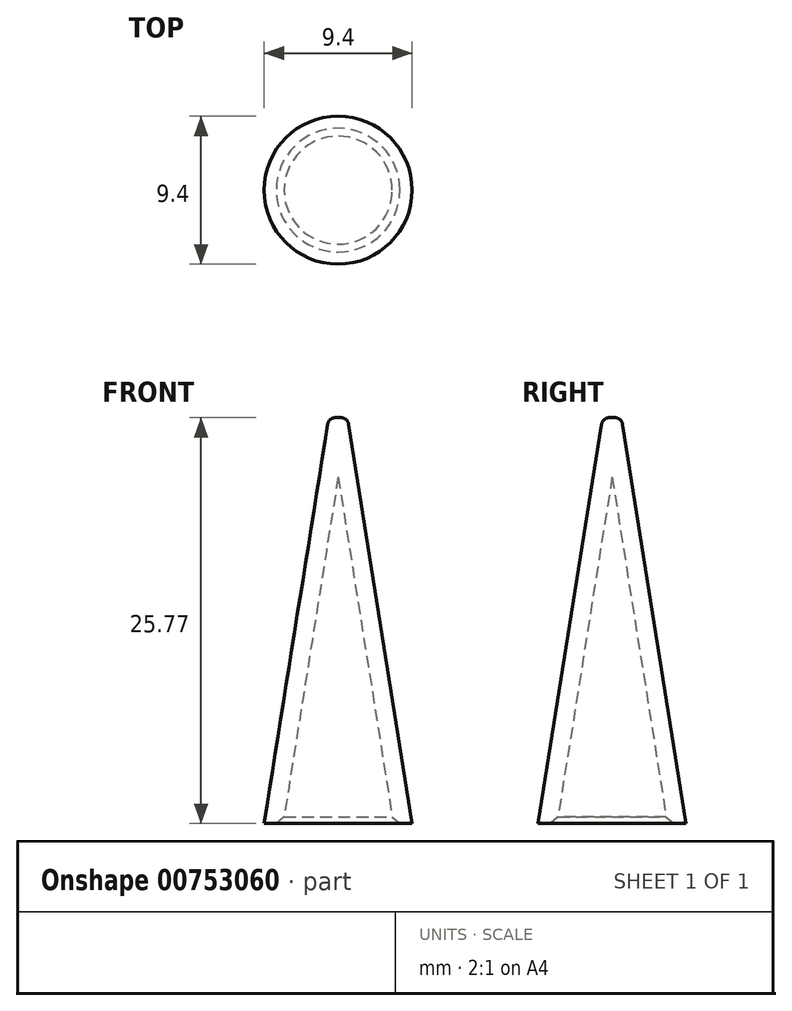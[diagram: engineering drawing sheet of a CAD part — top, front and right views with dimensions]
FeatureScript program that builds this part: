
annotation { "Feature Type Name" : "Feature", "Feature Type Description" : "" }
export const myFeature = defineFeature(function(context is Context, id is Id, definition is map)
    precondition{}
    {
        {
            var Q0;
            Q0=qCreatedBy(makeId("Front.planeOp"),FACE);
            var sketch = newSketch(context, id + "F0", { "sketchPlane" : qUnion([Q0])});
            skLineSegment(sketch, "E0", {"start": v(0, 0) * mm, "end": v(0, 29.54) * mm, "construction": true});
            skLineSegment(sketch, "E1", {"start": v(-3.5, 0) * mm, "end": v(0, 22) * mm});
            skLineSegment(sketch, "E2", {"start": v(0, 22) * mm, "end": v(0, 25.77) * mm});
            skLineSegment(sketch, "E3", {"start": v(-3.5, 0) * mm, "end": v(-4.7, 0) * mm});
            skLineSegment(sketch, "E4", {"start": v(-4.7, 0) * mm, "end": v(-0.6, 25.77) * mm});
            skLineSegment(sketch, "E5", {"start": v(0, 25.77) * mm, "end": v(-0.6, 25.77) * mm});
            skPoint(sketch, "E6.orphan", {"position": v(0, 29.54) * mm});
            skSolve(sketch);
        }
        {
            var Q0;
            Q0 = qSketchRegion(id + "F0", true);
            var Q1;
            Q1=sQuery(id+"F0.wireOp",EDGE,"E0");
            revolve(context, id + "F1", {"surfaceOperationType" : NewSurfaceOperationType.NEW, "entities" : qUnion([Q0]), "axis" : qUnion([Q1]), "revolveType" : RevolveType.FULL});
        }
        {
            var Q0;
            Q0=makeQuery(id+"F1.opRevolve","SWEPT_EDGE",EDGE,{"disambiguationData":[OSD([sQuery(id+"F0.wireOp",EDGE,"E4"),sQuery(id+"F0.wireOp",EDGE,"E5")])]});
            fillet(context, id + "F2", {"entities" : qUnion([Q0]), "radius" : .5 * mm, "tangentPropagation" : true, "allowEdgeOverflow" : false});
        }
        {
            var Q0;
            Q0=makeQuery(id+"F1.opRevolve","SWEPT_EDGE",EDGE,{"disambiguationData":[OSD([sQuery(id+"F0.wireOp",EDGE,"E1"),sQuery(id+"F0.wireOp",EDGE,"E3")])]});
            chamfer(context, id + "F3", {"entities" : qUnion([Q0]), "width" : .5 * mm, "tangentPropagation" : true});
        }
    });
